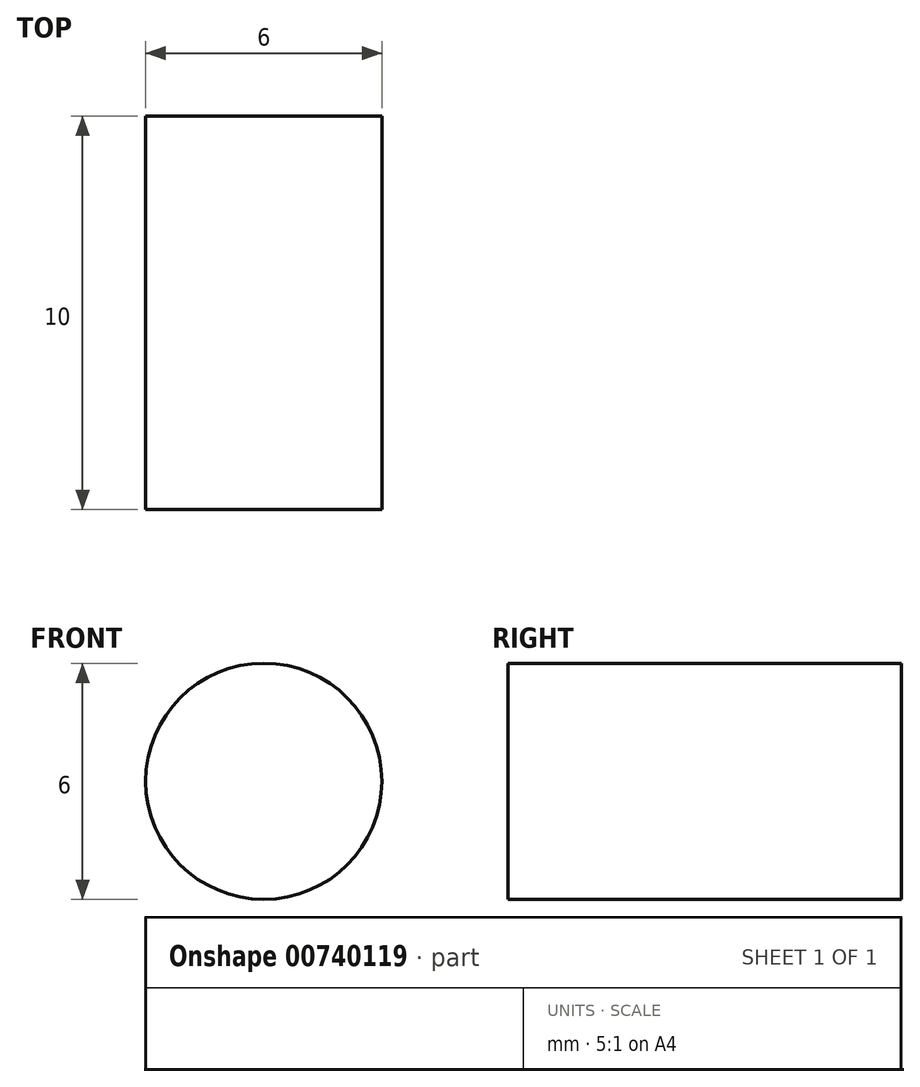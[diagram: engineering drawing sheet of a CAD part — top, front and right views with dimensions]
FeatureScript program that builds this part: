
annotation { "Feature Type Name" : "Feature", "Feature Type Description" : "" }
export const myFeature = defineFeature(function(context is Context, id is Id, definition is map)
    precondition{}
    {
        {
            var Q0;
            Q0=qCreatedBy(makeId("Front.planeOp"),FACE);
            var sketch = newSketch(context, id + "F0", { "sketchPlane" : qUnion([Q0])});
            skCircle(sketch, "E0", {"center": v(0, 0) * mm, "radius": 3 * mm});
            skSolve(sketch);
        }
        {
            var Q0;
            Q0=makeQuery(id+"F0.imprint","IMPRINT",FACE,{"disambiguationData":[TD([[makeQuery(id+"F0.imprint","IMPRINT",EDGE,{"derivedFrom":sQuery(id+"F0.wireOp",EDGE,"E0")}),1.0]])]});
            extrude(context, id + "F1", {"entities" : qUnion([Q0]), "depth" : 10 * mm, "offsetDistance" : 25 * mm});
        }
    });
